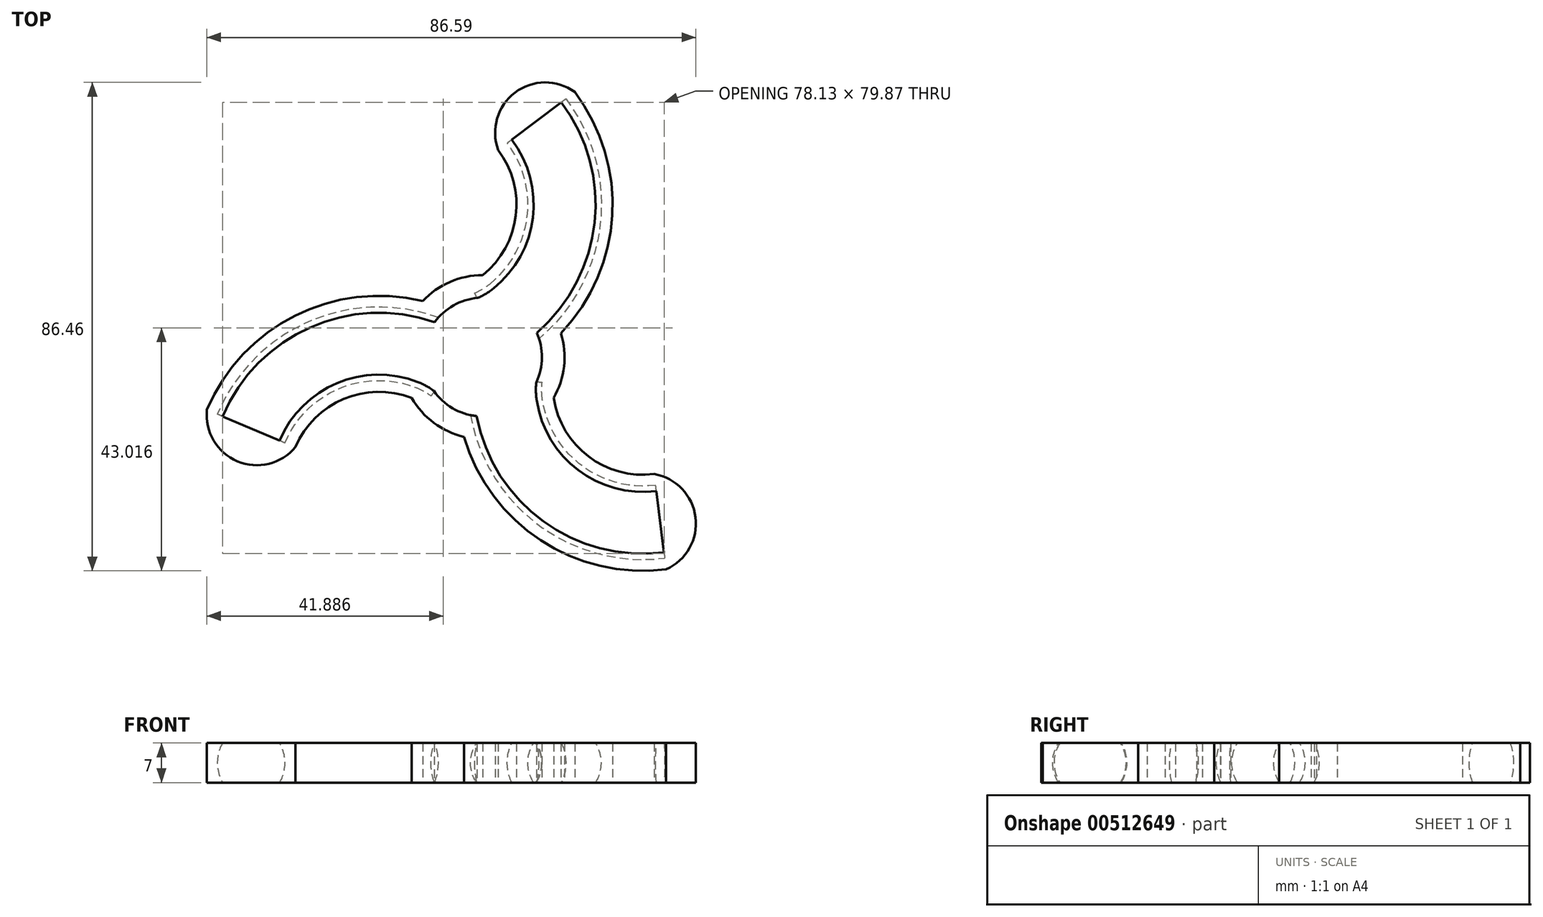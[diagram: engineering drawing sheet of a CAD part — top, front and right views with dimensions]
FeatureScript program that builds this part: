
annotation { "Feature Type Name" : "Feature", "Feature Type Description" : "" }
export const myFeature = defineFeature(function(context is Context, id is Id, definition is map)
    precondition{}
    {
        {
            var Q0;
            Q0=qCreatedBy(makeId("Top.planeOp"),FACE);
            var sketch = newSketch(context, id + "F0", { "sketchPlane" : qUnion([Q0])});
            skCircle(sketch, "E0", {"center": v(0, 0) * mm, "radius": 10.5 * mm});
            skCircle(sketch, "E1.0", {"center": v(0, 0) * mm, "radius": 14.5 * mm});
            skPoint(sketch, "E2.endSnap0", {"position": v(0, 27) * mm});
            skArc(sketch, "E3", {"start": v(0, 14.5) * mm, "mid": v(5.88, 25.02) * mm, "end": v(2.75, 36.67) * mm});
            skArc(sketch, "E4.0", {"start": v(10.63, 1.24) * mm, "mid": v(22.75, 22.93) * mm, "end": v(16.3, 46.93) * mm});
            skArc(sketch, "E5.0", {"start": v(5.32, 7.87) * mm, "mid": v(14.31, 23.98) * mm, "end": v(9.53, 41.8) * mm});
            skLineSegment(sketch, "E6", {"start": v(9.53, 41.8) * mm, "end": v(16.3, 46.93) * mm});
            skLineSegment(sketch, "E7", {"start": v(9.53, 41.8) * mm, "end": v(2.75, 36.67) * mm});
            skArc(sketch, "E8", {"start": v(16.3, 46.93) * mm, "mid": v(5.73, 46.82) * mm, "end": v(2.75, 36.67) * mm});
            skPoint(sketch, "E9.orphan", {"position": v(10.63, 52.76) * mm});
            skPoint(sketch, "E10.orphan", {"position": v(0, 39.5) * mm});
            skArc(sketch, "E11.1.0", {"start": v(-12.56, -7.25) * mm, "mid": v(-24.61, -7.42) * mm, "end": v(-33.13, -15.95) * mm});
            skArc(sketch, "E11.1.1", {"start": v(-9.47, 0.67) * mm, "mid": v(-27.92, 0.4) * mm, "end": v(-40.96, -12.64) * mm});
            skArc(sketch, "E11.1.2", {"start": v(-6.39, 8.6) * mm, "mid": v(-31.23, 8.24) * mm, "end": v(-48.8, -9.34) * mm});
            skLineSegment(sketch, "E11.1.3", {"start": v(-40.96, -12.64) * mm, "end": v(-48.8, -9.34) * mm});
            skArc(sketch, "E11.1.4", {"start": v(-48.8, -9.34) * mm, "mid": v(-43.41, -18.45) * mm, "end": v(-33.13, -15.95) * mm});
            skLineSegment(sketch, "E11.1.5", {"start": v(-40.96, -12.64) * mm, "end": v(-33.13, -15.95) * mm});
            skArc(sketch, "E11.2.0", {"start": v(12.56, -7.25) * mm, "mid": v(18.73, -17.6) * mm, "end": v(30.38, -20.72) * mm});
            skArc(sketch, "E11.2.1", {"start": v(4.16, -8.54) * mm, "mid": v(13.6, -24.38) * mm, "end": v(31.43, -29.15) * mm});
            skArc(sketch, "E11.2.2", {"start": v(-4.25, -9.83) * mm, "mid": v(8.48, -31.16) * mm, "end": v(32.49, -37.59) * mm});
            skLineSegment(sketch, "E11.2.3", {"start": v(31.43, -29.15) * mm, "end": v(32.49, -37.59) * mm});
            skArc(sketch, "E11.2.4", {"start": v(32.49, -37.59) * mm, "mid": v(37.69, -28.37) * mm, "end": v(30.38, -20.72) * mm});
            skLineSegment(sketch, "E11.2.5", {"start": v(31.43, -29.15) * mm, "end": v(30.38, -20.72) * mm});
            skArc(sketch, "E12", {"start": v(-9.47, 0.67) * mm, "mid": v(-7.26, -0.37) * mm, "end": v(-5.22, -1.7) * mm});
            skArc(sketch, "E13.1.0", {"start": v(4.16, -8.54) * mm, "mid": v(3.95, -6.1) * mm, "end": v(4.09, -3.67) * mm});
            skArc(sketch, "E13.2.0", {"start": v(5.32, 7.87) * mm, "mid": v(3.31, 6.48) * mm, "end": v(1.14, 5.37) * mm});
            skSolve(sketch);
        }
        {
            var Q0;
            {var subQ5=sQuery(id+"F0.wireOp",EDGE,"E11.1.3");Q0=makeQuery(id+"F0.imprint","IMPRINT",FACE,{"disambiguationData":[TD([[makeQuery(id+"F0.imprint","IMPRINT",EDGE,{"derivedFrom":subQ5}),-1.0]])]});}
            var Q1;
            {var subQ0=sQuery(id+"F0.wireOp",EDGE,"E11.1.0");Q1=makeQuery(id+"F0.imprint","IMPRINT",FACE,{"disambiguationData":[TD([[makeQuery(id+"F0.imprint","IMPRINT",EDGE,{"derivedFrom":subQ0}),-1.0]])]});}
            var Q2;
            {var subQ4=sQuery(id+"F0.wireOp",EDGE,"E11.1.1");var subQ5=sQuery(id+"F0.wireOp",EDGE,"E0");var subQ6=makeQuery(id+"F0.imprint","INTERSECT",VERTEX,{"derivedFrom":[subQ5,subQ4]});Q2=makeQuery(id+"F0.imprint","IMPRINT",FACE,{"disambiguationData":[TD([[makeQuery(id+"F0.imprint","IMPRINT",EDGE,{"disambiguationData":[TD([[subQ6,-1.0]])],"derivedFrom":subQ5}),-1.0]])]});}
            var Q3;
            {var subQ2=sQuery(id+"F0.wireOp",EDGE,"E11.1.1");var subQ7=sQuery(id+"F0.wireOp",EDGE,"E0");var subQ8=makeQuery(id+"F0.imprint","INTERSECT",VERTEX,{"derivedFrom":[subQ7,subQ2]});Q3=makeQuery(id+"F0.imprint","IMPRINT",FACE,{"disambiguationData":[TD([[makeQuery(id+"F0.imprint","IMPRINT",EDGE,{"disambiguationData":[TD([[subQ8,1.0]])],"derivedFrom":subQ7}),-1.0]])]});}
            var Q4;
            {var subQ0=sQuery(id+"F0.wireOp",EDGE,"E3");Q4=makeQuery(id+"F0.imprint","IMPRINT",FACE,{"disambiguationData":[TD([[makeQuery(id+"F0.imprint","IMPRINT",EDGE,{"derivedFrom":subQ0}),-1.0]])]});}
            var Q5;
            {var subQ5=sQuery(id+"F0.wireOp",EDGE,"E6");Q5=makeQuery(id+"F0.imprint","IMPRINT",FACE,{"disambiguationData":[TD([[makeQuery(id+"F0.imprint","IMPRINT",EDGE,{"derivedFrom":subQ5}),-1.0]])]});}
            var Q6;
            {var subQ5=sQuery(id+"F0.wireOp",EDGE,"E5.0");var subQ7=sQuery(id+"F0.wireOp",EDGE,"E0");var subQ8=makeQuery(id+"F0.imprint","INTERSECT",VERTEX,{"derivedFrom":[subQ7,subQ5]});Q6=makeQuery(id+"F0.imprint","IMPRINT",FACE,{"disambiguationData":[TD([[makeQuery(id+"F0.imprint","IMPRINT",EDGE,{"disambiguationData":[TD([[subQ8,1.0]])],"derivedFrom":subQ7}),-1.0]])]});}
            var Q7;
            {var subQ0=sQuery(id+"F0.wireOp",EDGE,"E11.2.0");Q7=makeQuery(id+"F0.imprint","IMPRINT",FACE,{"disambiguationData":[TD([[makeQuery(id+"F0.imprint","IMPRINT",EDGE,{"derivedFrom":subQ0}),-1.0]])]});}
            var Q8;
            {var subQ5=sQuery(id+"F0.wireOp",EDGE,"E11.2.3");Q8=makeQuery(id+"F0.imprint","IMPRINT",FACE,{"disambiguationData":[TD([[makeQuery(id+"F0.imprint","IMPRINT",EDGE,{"derivedFrom":subQ5}),-1.0]])]});}
            extrude(context, id + "F1", {"entities" : qUnion([Q0, Q1, Q2, Q3, Q4, Q5, Q6, Q7, Q8]), "endBound" : BoundingType.SYMMETRIC, "depth" : 7 * mm});
        }
        {
            var Q0;
            Q0=makeQuery(id+"F1.opExtrude","SWEPT_FACE",FACE,{"disambiguationData":[OSD([sQuery(id+"F0.wireOp",EDGE,"E11.1.3"),sQuery(id+"F0.wireOp",EDGE,"E11.1.5")])]});
            cPlane(context, id + "F2", {"entities" : qUnion([Q0]), "cplaneType" : CPlaneType.OFFSET, "offset" : 0 * mm, "width" : 150 * mm, "height" : 150 * mm});
        }
        {
            var Q0;
            Q0=qCreatedBy(id+"F2.planeOp",FACE);
            var sketch = newSketch(context, id + "F3", { "sketchPlane" : qUnion([Q0])});
            skCircle(sketch, "E14", {"center": v(-32.83, 0) * mm, "radius": 6.5 * mm});
            skSolve(sketch);
        }
        {
            var Q0;
            Q0=makeQuery(id+"F3.imprint","IMPRINT",FACE,{"disambiguationData":[TD([[makeQuery(id+"F3.imprint","IMPRINT",EDGE,{"derivedFrom":sQuery(id+"F3.wireOp",EDGE,"E14")}),1.0]])]});
            var Q1;
            Q1=sQuery(id+"F0.wireOp",EDGE,"E11.1.1");
            var Q2;
            Q2=sQuery(id+"F0.wireOp",EDGE,"E12");
            sweep(context, id + "F4", {"operationType" : NewBodyOperationType.REMOVE, "profiles" : qUnion([Q0]), "path" : qUnion([Q1, Q2])});
        }
        {
            var Q0;
            Q0=makeQuery(id+"F1.opExtrude","SWEPT_FACE",FACE,{"disambiguationData":[OSD([sQuery(id+"F0.wireOp",EDGE,"E11.2.3"),sQuery(id+"F0.wireOp",EDGE,"E11.2.5")])]});
            cPlane(context, id + "F5", {"entities" : qUnion([Q0]), "cplaneType" : CPlaneType.OFFSET, "offset" : 0 * mm, "width" : 150 * mm, "height" : 150 * mm});
        }
        {
            var Q0;
            Q0=qCreatedBy(id+"F5.planeOp",FACE);
            var sketch = newSketch(context, id + "F6", { "sketchPlane" : qUnion([Q0])});
            skCircle(sketch, "E15", {"center": v(-32.82, 0) * mm, "radius": 6.5 * mm});
            skSolve(sketch);
        }
        {
            var Q0;
            Q0=makeQuery(id+"F6.imprint","IMPRINT",FACE,{"disambiguationData":[TD([[makeQuery(id+"F6.imprint","IMPRINT",EDGE,{"derivedFrom":sQuery(id+"F6.wireOp",EDGE,"E15")}),1.0]])]});
            var Q1;
            Q1=sQuery(id+"F6.wireOp",EDGE,"E15");
            var Q2;
            Q2=sQuery(id+"F0.wireOp",EDGE,"E11.2.1");
            var Q3;
            Q3=sQuery(id+"F0.wireOp",EDGE,"E13.1.0");
            sweep(context, id + "F7", {"operationType" : NewBodyOperationType.REMOVE, "profiles" : qUnion([Q0]), "surfaceProfiles" : qUnion([Q1]), "path" : qUnion([Q2, Q3])});
        }
        {
            var Q0;
            Q0=makeQuery(id+"F1.opExtrude","SWEPT_FACE",FACE,{"disambiguationData":[OSD([sQuery(id+"F0.wireOp",EDGE,"E6"),sQuery(id+"F0.wireOp",EDGE,"E7")])]});
            cPlane(context, id + "F8", {"entities" : qUnion([Q0]), "cplaneType" : CPlaneType.OFFSET, "offset" : 0 * mm, "width" : 150 * mm, "height" : 150 * mm});
        }
        {
            var Q0;
            Q0=qCreatedBy(id+"F8.planeOp",FACE);
            var sketch = newSketch(context, id + "F9", { "sketchPlane" : qUnion([Q0])});
            skCircle(sketch, "E16", {"center": v(-32.84, 0) * mm, "radius": 6.5 * mm});
            skSolve(sketch);
        }
        {
            var Q0;
            Q0=makeQuery(id+"F9.imprint","IMPRINT",FACE,{"disambiguationData":[TD([[makeQuery(id+"F9.imprint","IMPRINT",EDGE,{"derivedFrom":sQuery(id+"F9.wireOp",EDGE,"E16")}),1.0]])]});
            var Q1;
            Q1=sQuery(id+"F0.wireOp",EDGE,"E5.0");
            var Q2;
            Q2=sQuery(id+"F0.wireOp",EDGE,"E13.2.0");
            sweep(context, id + "F10", {"operationType" : NewBodyOperationType.REMOVE, "profiles" : qUnion([Q0]), "path" : qUnion([Q1, Q2])});
        }
        {
            var Q0;
            Q0=makeQuery(id+"F0.imprint","IMPRINT",FACE,{"disambiguationData":[TD([[makeQuery(id+"F0.imprint","IMPRINT",EDGE,{"derivedFrom":sQuery(id+"F0.wireOp",EDGE,"E6")}),1.0]])]});
            var Q1;
            Q1=makeQuery(id+"F0.imprint","IMPRINT",FACE,{"disambiguationData":[TD([[makeQuery(id+"F0.imprint","IMPRINT",EDGE,{"derivedFrom":sQuery(id+"F0.wireOp",EDGE,"E11.1.3")}),1.0]])]});
            var Q2;
            Q2=makeQuery(id+"F0.imprint","IMPRINT",FACE,{"disambiguationData":[TD([[makeQuery(id+"F0.imprint","IMPRINT",EDGE,{"derivedFrom":sQuery(id+"F0.wireOp",EDGE,"E11.2.3")}),1.0]])]});
            extrude(context, id + "F11", {"entities" : qUnion([Q0, Q1, Q2]), "operationType" : NewBodyOperationType.ADD, "endBound" : BoundingType.SYMMETRIC, "depth" : 7 * mm});
        }
    });
